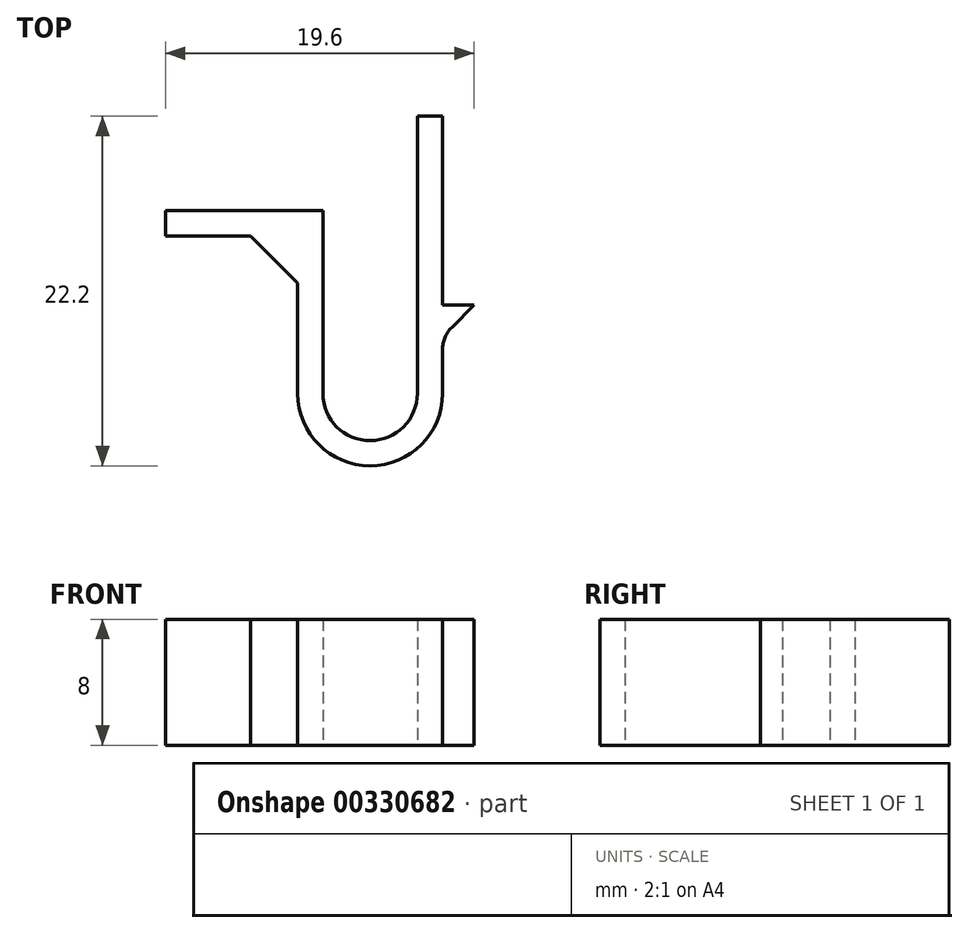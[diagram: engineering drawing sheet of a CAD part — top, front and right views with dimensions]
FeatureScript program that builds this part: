
annotation { "Feature Type Name" : "Feature", "Feature Type Description" : "" }
export const myFeature = defineFeature(function(context is Context, id is Id, definition is map)
    precondition{}
    {
        {
            var Q0;
            Q0=qCreatedBy(makeId("Top.planeOp"),FACE);
            var sketch = newSketch(context, id + "F0", { "sketchPlane" : qUnion([Q0])});
            skLineSegment(sketch, "E0.bottom", {"start": v(0, 0) * mm, "end": v(1.6, 0) * mm});
            skLineSegment(sketch, "E0.top", {"start": v(0, 10) * mm, "end": v(1.6, 10) * mm});
            skLineSegment(sketch, "E0.left", {"start": v(0, 0) * mm, "end": v(0, 10) * mm});
            skLineSegment(sketch, "E0.right", {"start": v(1.6, 0) * mm, "end": v(1.6, 10) * mm});
            skLineSegment(sketch, "E1.bottom", {"start": v(7.6, 0) * mm, "end": v(9.2, 0) * mm});
            skLineSegment(sketch, "E1.top", {"start": v(7.6, 17.6) * mm, "end": v(9.2, 17.6) * mm});
            skLineSegment(sketch, "E1.left", {"start": v(7.6, 0) * mm, "end": v(7.6, 17.6) * mm});
            skLineSegment(sketch, "E1.right", {"start": v(9.2, 0) * mm, "end": v(9.2, 17.6) * mm});
            skLineSegment(sketch, "E2.bottom", {"start": v(1.6, 10) * mm, "end": v(-8.4, 10) * mm});
            skLineSegment(sketch, "E2.top", {"start": v(1.6, 11.6) * mm, "end": v(-8.4, 11.6) * mm});
            skLineSegment(sketch, "E2.left", {"start": v(1.6, 10) * mm, "end": v(1.6, 11.6) * mm});
            skLineSegment(sketch, "E2.right", {"start": v(-8.4, 10) * mm, "end": v(-8.4, 11.6) * mm});
            skArc(sketch, "E3", {"start": v(0, 0) * mm, "mid": v(4.6, -4.6) * mm, "end": v(9.2, 0) * mm});
            skArc(sketch, "E4", {"start": v(1.6, 0) * mm, "mid": v(4.6, -3) * mm, "end": v(7.6, 0) * mm});
            skPoint(sketch, "E5.endSnap0", {"position": v(9.2, 7.3) * mm});
            skLineSegment(sketch, "E6", {"start": v(9.2, 5.6) * mm, "end": v(11.2, 5.6) * mm});
            skLineSegment(sketch, "E7", {"start": v(11.2, 5.6) * mm, "end": v(9.2, 3.6) * mm});
            skSolve(sketch);
        }
        {
            var Q0;
            {var subQ0=sQuery(id+"F0.wireOp",EDGE,"E6");Q0=makeQuery(id+"F0.imprint","IMPRINT",FACE,{"disambiguationData":[TD([[makeQuery(id+"F0.imprint","IMPRINT",EDGE,{"derivedFrom":subQ0}),-1.0]])]});}
            var Q1;
            {var subQ1=sQuery(id+"F0.wireOp",EDGE,"E1.bottom");Q1=makeQuery(id+"F0.imprint","IMPRINT",FACE,{"disambiguationData":[TD([[makeQuery(id+"F0.imprint","IMPRINT",EDGE,{"derivedFrom":subQ1}),1.0]])]});}
            var Q2;
            Q2=makeQuery(id+"F0.imprint","IMPRINT",FACE,{"disambiguationData":[TD([[makeQuery(id+"F0.imprint","IMPRINT",EDGE,{"derivedFrom":sQuery(id+"F0.wireOp",EDGE,"E0.bottom")}),-1.0]])]});
            var Q3;
            Q3=makeQuery(id+"F0.imprint","IMPRINT",FACE,{"disambiguationData":[TD([[makeQuery(id+"F0.imprint","IMPRINT",EDGE,{"derivedFrom":sQuery(id+"F0.wireOp",EDGE,"E0.bottom")}),1.0]])]});
            var Q4;
            Q4=makeQuery(id+"F0.imprint","IMPRINT",FACE,{"disambiguationData":[TD([[makeQuery(id+"F0.imprint","IMPRINT",EDGE,{"derivedFrom":sQuery(id+"F0.wireOp",EDGE,"E2.top")}),1.0]])]});
            extrude(context, id + "F1", {"entities" : qUnion([Q0, Q1, Q2, Q3, Q4]), "depth" : 8 * mm});
        }
        {
            var Q0;
            Q0=makeQuery(id+"F1.opExtrude","SWEPT_EDGE",EDGE,{"disambiguationData":[OSD([sQuery(id+"F0.wireOp",EDGE,"E1.right"),sQuery(id+"F0.wireOp",EDGE,"E7")])]});
            fillet(context, id + "F2", {"entities" : qUnion([Q0]), "radius" : 2 * mm, "tangentPropagation" : true, "allowEdgeOverflow" : false});
        }
        {
            var Q0;
            Q0=makeQuery(id+"F1.opExtrude","SWEPT_EDGE",EDGE,{"disambiguationData":[OSD([sQuery(id+"F0.wireOp",EDGE,"E0.left"),sQuery(id+"F0.wireOp",EDGE,"E2.bottom")])]});
            chamfer(context, id + "F3", {"entities" : qUnion([Q0]), "width" : 3 * mm, "tangentPropagation" : true});
        }
    });
